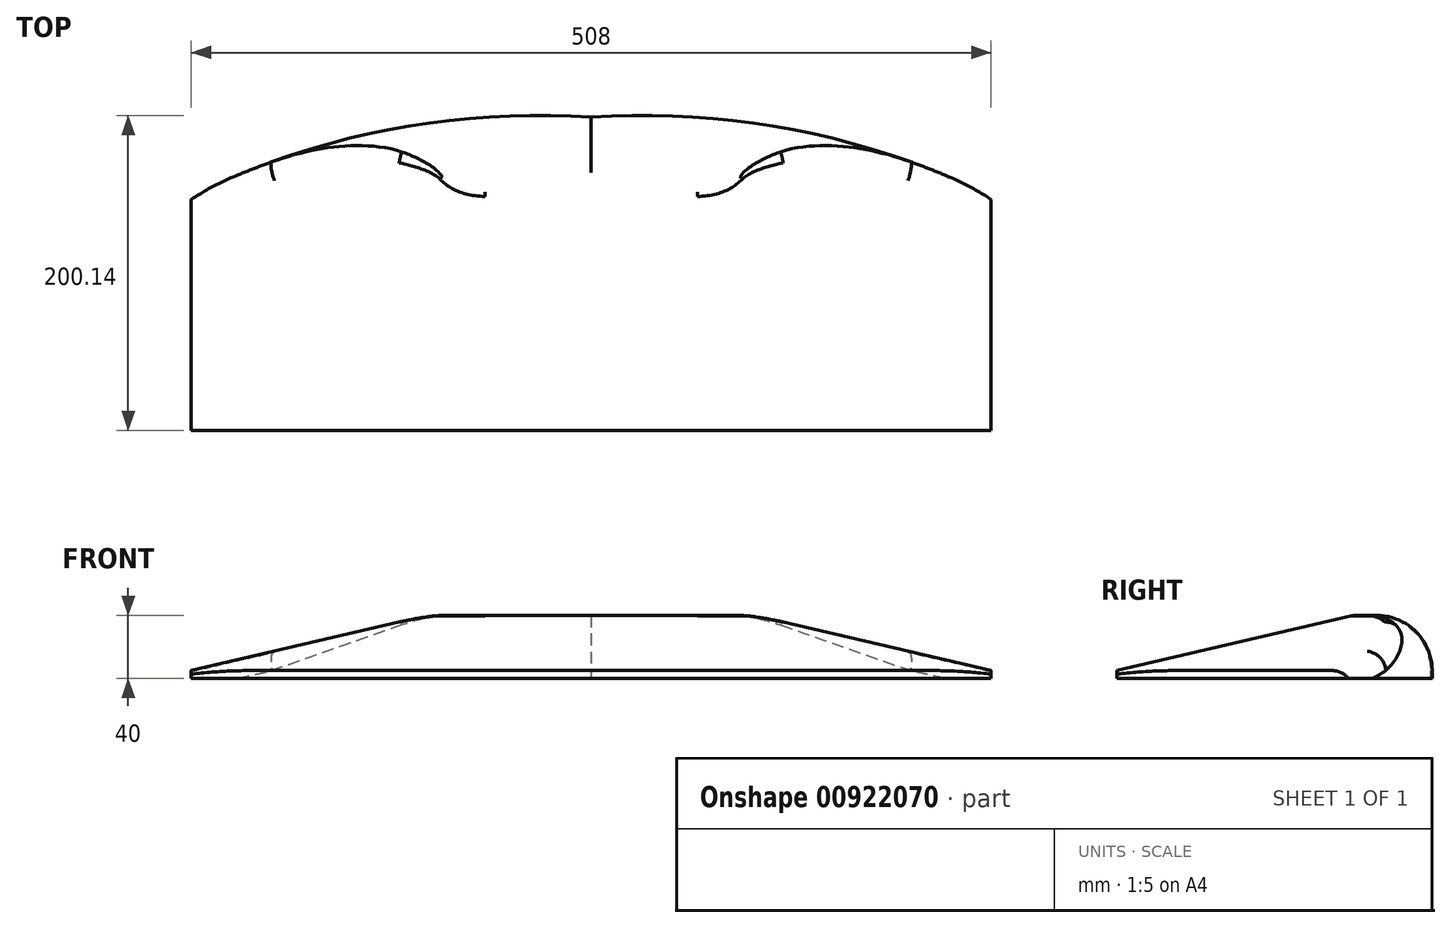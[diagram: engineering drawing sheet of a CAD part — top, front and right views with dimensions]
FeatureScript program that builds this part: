
annotation { "Feature Type Name" : "Feature", "Feature Type Description" : "" }
export const myFeature = defineFeature(function(context is Context, id is Id, definition is map)
    precondition{}
    {
        {
            var Q0;
            Q0=qCreatedBy(makeId("Top.planeOp"),FACE);
            var sketch = newSketch(context, id + "F0", { "sketchPlane" : qUnion([Q0])});
            skLineSegment(sketch, "E0", {"start": v(0, 0) * mm, "end": v(0, 100) * mm});
            skLineSegment(sketch, "E1", {"start": v(0, 0) * mm, "end": v(0, -99) * mm});
            skLineSegment(sketch, "E2", {"start": v(254, 0) * mm, "end": v(254, 50) * mm});
            skPoint(sketch, "E2.endSnap0", {"position": v(0, 50) * mm});
            skLineSegment(sketch, "E3", {"start": v(254, 0) * mm, "end": v(254, -99) * mm});
            skArc(sketch, "E4", {"start": v(254, 50) * mm, "mid": v(130.3, 91.72) * mm, "end": v(0, 100) * mm});
            skLineSegment(sketch, "E5", {"start": v(254, -99) * mm, "end": v(0, -99) * mm});
            skPoint(sketch, "E6.orphan", {"position": v(250.1, -99) * mm});
            skPoint(sketch, "E7.orphan", {"position": v(254, -100) * mm});
            skLineSegment(sketch, "E8", {"start": v(0, 100) * mm, "end": v(0, 125) * mm});
            skSolve(sketch);
        }
        {
            var Q0;
            Q0=makeQuery(id+"F0.imprint","IMPRINT",FACE,{"disambiguationData":[TD([[makeQuery(id+"F0.imprint","IMPRINT",EDGE,{"derivedFrom":sQuery(id+"F0.wireOp",EDGE,"E0")}),-1.0]])]});
            extrude(context, id + "F1", {"entities" : qUnion([Q0]), "depth" : 40 * mm, "offsetDistance" : 25 * mm});
        }
        {
            var Q0;
            Q0=makeQuery(id+"F1.opExtrude","CAP_EDGE",EDGE,{"disambiguationData":[OSD([sQuery(id+"F0.wireOp",EDGE,"E5")])],"isStart":false});
            var Q1;
            Q1=makeQuery(id+"F1.opExtrude","CAP_EDGE",EDGE,{"disambiguationData":[OSD([sQuery(id+"F0.wireOp",EDGE,"E2"),sQuery(id+"F0.wireOp",EDGE,"E3")])],"isStart":false});
            chamfer(context, id + "F2", {"entities" : qUnion([Q0, Q1]), "chamferType" : ChamferType.TWO_OFFSETS, "width1" : 150 * mm, "oppositeDirection" : true, "width2" : 35 * mm, "tangentPropagation" : true});
        }
        {
            var Q0;
            Q0=makeQuery(id+"F1.opExtrude","CAP_EDGE",EDGE,{"disambiguationData":[OSD([sQuery(id+"F0.wireOp",EDGE,"E4")])],"isStart":false});
            fillet(context, id + "F3", {"entities" : qUnion([Q0]), "radius" : 35 * mm, "tangentPropagation" : true, "allowEdgeOverflow" : false});
        }
        {
            var Q0;
            Q0=makeQuery(id+"F2.opChamfer","BLEND_EDGE",EDGE,{"blendedFrom":[makeQuery(id+"F1.opExtrude","CAP_EDGE",EDGE,{"disambiguationData":[OSD([sQuery(id+"F0.wireOp",EDGE,"E2"),sQuery(id+"F0.wireOp",EDGE,"E3")])],"isStart":false}),makeQuery(id+"F1.opExtrude","CAP_EDGE",EDGE,{"disambiguationData":[OSD([sQuery(id+"F0.wireOp",EDGE,"E5")])],"isStart":false})],"blendedInto":[]});
            fillet(context, id + "F4", {"entities" : qUnion([Q0]), "radius" : 167.13 * mm, "tangentPropagation" : true, "allowEdgeOverflow" : false});
        }
        {
            var Q0;
            Q0=makeQuery(id+"F3.opFillet","BLEND_EDGE",EDGE,{"blendedFrom":[makeQuery(id+"F1.opExtrude","CAP_EDGE",EDGE,{"disambiguationData":[OSD([sQuery(id+"F0.wireOp",EDGE,"E4")])],"isStart":false}),makeQuery(id+"F2.opChamfer","BLEND_FACE",FACE,{"disambiguationData":[OSD([sQuery(id+"F0.wireOp",EDGE,"E2"),sQuery(id+"F0.wireOp",EDGE,"E3")])]})],"blendedInto":[makeQuery(id+"F2.opChamfer","BLEND_FACE",FACE,{"disambiguationData":[OSD([sQuery(id+"F0.wireOp",EDGE,"E2"),sQuery(id+"F0.wireOp",EDGE,"E3")])]})]});
            fillet(context, id + "F5", {"entities" : qUnion([Q0]), "radius" : 12.63 * mm, "tangentPropagation" : true, "allowEdgeOverflow" : false});
        }
        {
            var Q0;
            Q0=makeQuery(id+"F1.opExtrude","SWEPT_BODY",BODY,{"disambiguationData":[OSD([sQuery(id+"F0.wireOp",EDGE,"E0"),sQuery(id+"F0.wireOp",EDGE,"E2"),sQuery(id+"F0.wireOp",EDGE,"E3"),sQuery(id+"F0.wireOp",EDGE,"E4"),sQuery(id+"F0.wireOp",EDGE,"E5"),sQuery(id+"F0.wireOp",EDGE,"E1")])]});
            var Q1;
            Q1=makeQuery(id+"F1.opExtrude","SWEPT_FACE",FACE,{"disambiguationData":[OSD([sQuery(id+"F0.wireOp",EDGE,"E0"),sQuery(id+"F0.wireOp",EDGE,"E1")])]});
            mirror(context, id + "F6", {"operationType" : NewBodyOperationType.ADD, "entities" : qUnion([Q0]), "mirrorPlane" : qUnion([Q1])});
        }
    });
